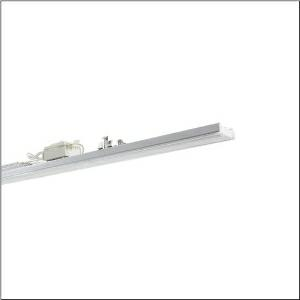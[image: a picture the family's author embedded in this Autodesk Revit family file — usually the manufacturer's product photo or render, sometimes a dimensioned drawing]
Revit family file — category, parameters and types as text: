
# Revit family: licross_21_recessed_mo_52tl10cn49xg
name_source: partatom
category: Lighting Fixtures
units: mm (PartAtom-declared; Revit-internal decimal feet)

## family parameters
Cut with Voids When Loaded = No
Host = Face
Light Source = No
Part Type = Normal
Room Calculation Point = No
Round Connector Dimension = Use Diameter
Shared = No

## types (1)
- --- (1 x LED, 9010 lm, 49.9 W, 4000K)
    Apparent Load = 50 VA
    CIE Flux Codes = 50 81 96 100 100
    Color Rendering = 80
    Color Temperature = 4000K
    Default Elevation = 1800 mm
    Description = Licross 21 Recessed MO, luminaire insert, of sheet steel, galvanised, coil coated, white, length: 1.500mm, width: 66mm, height: 67mm, LED rated luminous flux: 9.010lm, light colour: 840, SDCM (Standard Deviation of Colour Matching)MacAdam ≤ 3 SDCM (initial), control gear: ON/OFF Multilumen, CLOi, with plug, 3-pole, with phase selection, mains connection: 220..240V, AC, 50/60Hz, start of lifetime: 49W, end of service life: 61W, internal wiring halogen-free, primary optical cover: cover, of PMMA, light emission: direct distribution, primary light characteristic: symmetric, protection rating (complete): IP40, insulation class (complete): insulation class I (protective earthing), certification: CE, ENEC, VDE, UKCA, protection symbol: D if used in an environment without relevant dust loads with corresponding accessories, impact resistance: IK06, permissible ambient temperature for indoor applications: -35..+40°C, corresponds to IFS (International Featured Standards) requirements for safety and quality in the food industry, reducing of maximum allowable ambient temperature of 5°C with ceiling mounting, LABS conformity tested according to VDMA 24364:2018-05, The light source and the operating device comply with the requirements of the Ecodesign Regulation (EU) 2019/2020 and are replaceable in accordance with this regulation, packaging unit: 1 piece
    Height = 58 mm
    Lamp = 1 x LED
    Lamp Light Flux = 9010 lm
    Lamp Power = 49.9 W
    Lamp count = 1
    Length = 1500 mm
    Luminous efficacy = 181 lm/W
    Manufacturer = Siteco
    ModVariant = No
    Model = 52TL10CN49XG
    Mounting Place = Ceiling
    Mounting Type = Pendant
    Number of Poles = 1
    OnlyDefault = Yes
    Power Factor = 1
    Product Name = Licross 21 Recessed MO
    Product group = luminaire insert | ceiling pendant
    ProductGroupID = 901
    Protection Class = Protection class I
    Protection Degree = IP 40
    RLX_Detail_Level = 1
    RLX_Emergency_Light_Flux = 0 lm
    RLX_Emergency_Type = 0
    RLX_Emergency_Type_DB = No
    RlxData = <blob elided: 22437 chars, md5=5a8427a6>
    Socket = socket
    Standby Power = 0 W
    System Light Flux = 9010 lm
    System Power = 50 W
    Type Comments = factory setting: luminous flux: 100 % | (A | C | E) | 116 mA
    Type Image = l_1296930.jpg
    URL = http://relux.com
    VarID = @adj_110697
    Voltage = 0 V
    Weight = 0.00 kg
    Width = 66 mm

## geometry (parser evidence)
native form markers: Blend x4, Sweep x12
no freeform markers — native parametric forms only
